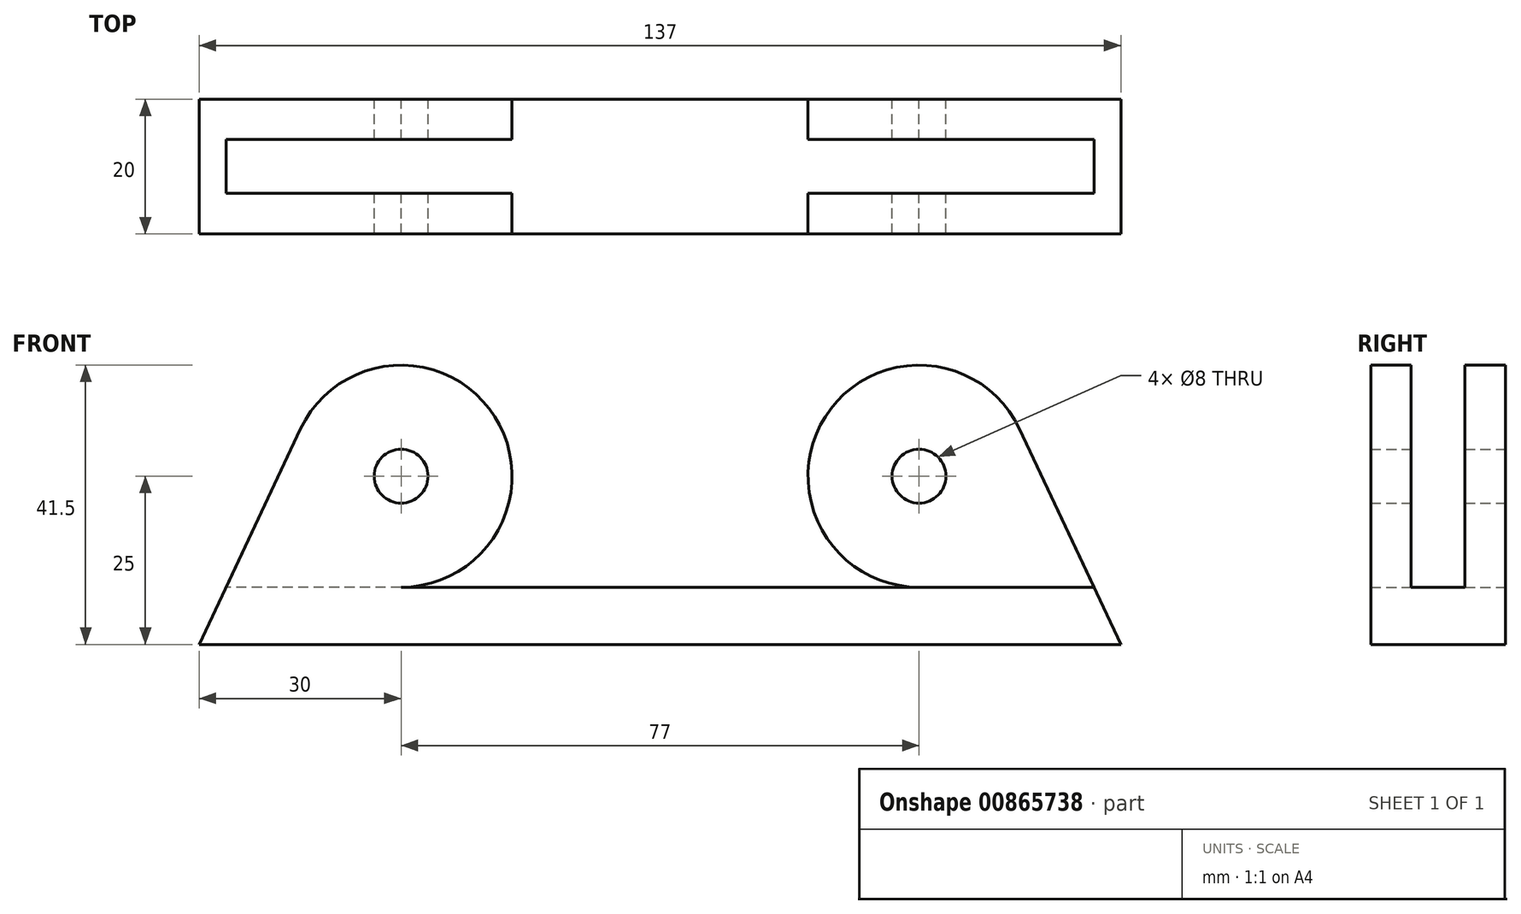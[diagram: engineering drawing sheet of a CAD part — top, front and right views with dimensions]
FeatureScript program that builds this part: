
annotation { "Feature Type Name" : "Feature", "Feature Type Description" : "" }
export const myFeature = defineFeature(function(context is Context, id is Id, definition is map)
    precondition{}
    {
        {
            var Q0;
            Q0=qCreatedBy(makeId("Front.planeOp"),FACE);
            var sketch = newSketch(context, id + "F0", { "sketchPlane" : qUnion([Q0])});
            skArc(sketch, "E0", {"start": v(0, -16.5) * mm, "mid": v(13.93, 8.84) * mm, "end": v(-14.93, 7.03) * mm});
            skArc(sketch, "E1", {"start": v(91.93, 7.03) * mm, "mid": v(63.07, 8.84) * mm, "end": v(77, -16.5) * mm});
            skLineSegment(sketch, "E2", {"start": v(-30, -25) * mm, "end": v(107, -25) * mm});
            skLineSegment(sketch, "E3", {"start": v(0, -16.5) * mm, "end": v(77, -16.5) * mm});
            skLineSegment(sketch, "E4", {"start": v(-30, -25) * mm, "end": v(-14.93, 7.03) * mm});
            skLineSegment(sketch, "E5", {"start": v(107, -25) * mm, "end": v(91.93, 7.03) * mm});
            skCircle(sketch, "E6", {"center": v(0, 0) * mm, "radius": 4 * mm});
            skCircle(sketch, "E7", {"center": v(77, 0) * mm, "radius": 4 * mm});
            skSolve(sketch);
        }
        {
            var Q0;
            Q0=makeQuery(id+"F0.imprint","IMPRINT",FACE,{"disambiguationData":[TD([[makeQuery(id+"F0.imprint","IMPRINT",EDGE,{"derivedFrom":sQuery(id+"F0.wireOp",EDGE,"E0")}),1.0]])]});
            extrude(context, id + "F1", {"entities" : qUnion([Q0]), "depth" : 20 * mm, "offsetDistance" : 25 * mm});
        }
        {
            var Q0;
            Q0=qCreatedBy(makeId("Right.planeOp"),FACE);
            var sketch = newSketch(context, id + "F2", { "sketchPlane" : qUnion([Q0])});
            skLineSegment(sketch, "E8.bottom", {"start": v(-14, -16.5) * mm, "end": v(-6, -16.5) * mm});
            skLineSegment(sketch, "E8.top", {"start": v(-14, 43.8) * mm, "end": v(-6, 43.8) * mm});
            skLineSegment(sketch, "E8.left", {"start": v(-14, -16.5) * mm, "end": v(-14, 43.8) * mm});
            skLineSegment(sketch, "E8.right", {"start": v(-6, -16.5) * mm, "end": v(-6, 43.8) * mm});
            skSolve(sketch);
        }
        {
            var Q0;
            Q0=makeQuery(id+"F2.imprint","IMPRINT",FACE,{"disambiguationData":[TD([[makeQuery(id+"F2.imprint","IMPRINT",EDGE,{"derivedFrom":sQuery(id+"F2.wireOp",EDGE,"E8.bottom")}),1.0]])]});
            extrude(context, id + "F3", {"entities" : qUnion([Q0]), "operationType" : NewBodyOperationType.REMOVE, "depth" : 128.3 * mm, "offsetDistance" : 25 * mm, "hasSecondDirection" : true, "secondDirectionOppositeDirection" : true, "secondDirectionDepth" : 41.8 * mm});
        }
    });
